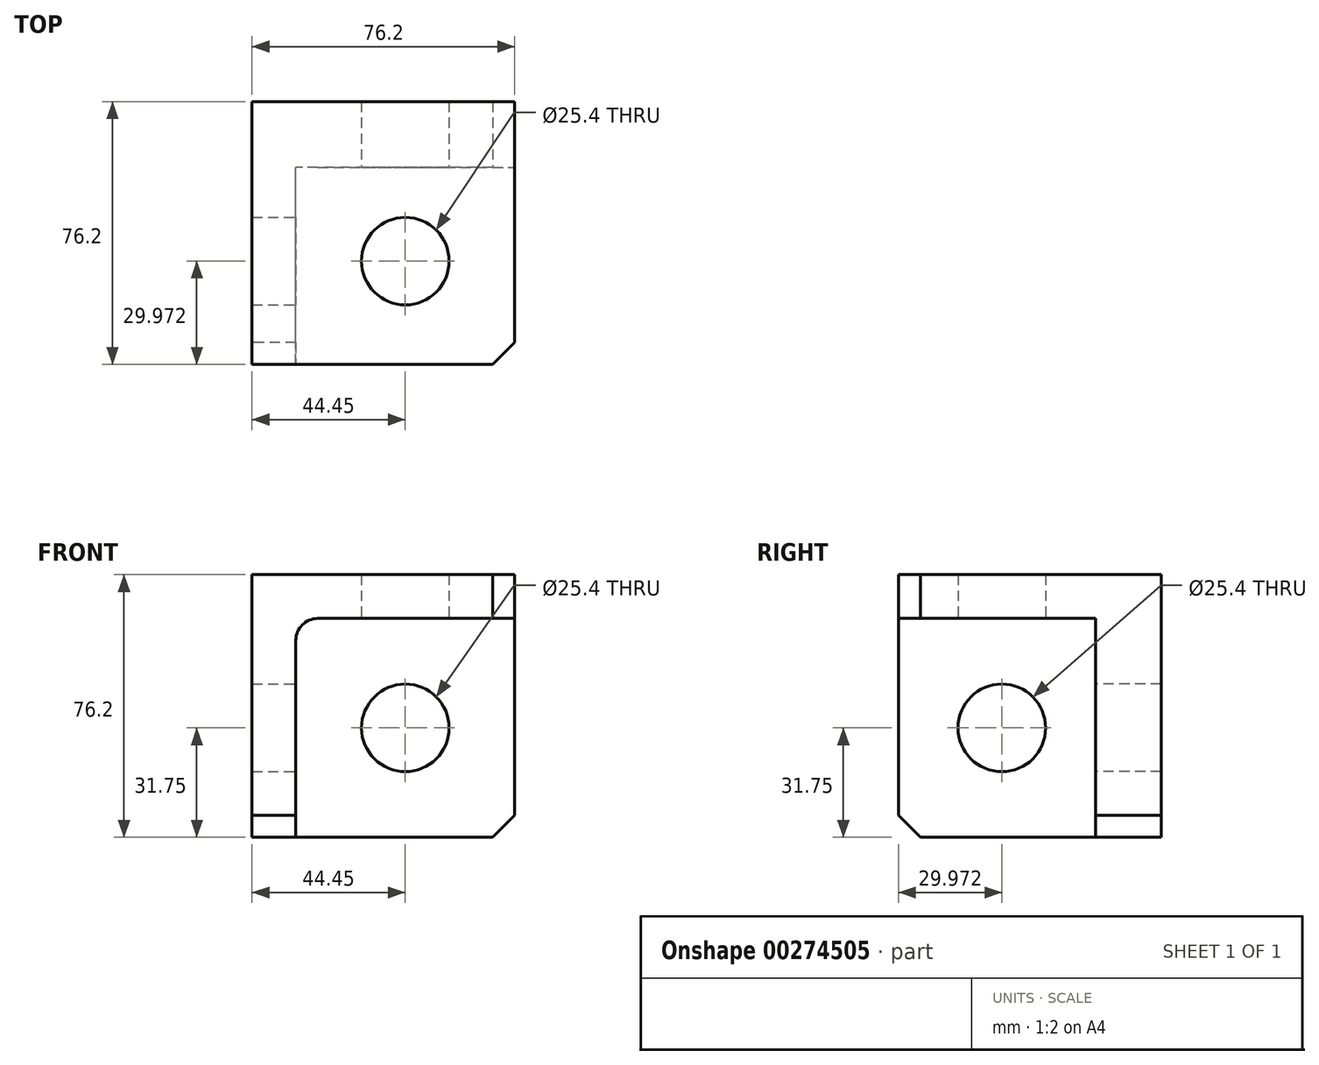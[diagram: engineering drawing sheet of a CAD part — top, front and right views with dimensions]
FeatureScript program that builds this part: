
annotation { "Feature Type Name" : "Feature", "Feature Type Description" : "" }
export const myFeature = defineFeature(function(context is Context, id is Id, definition is map)
    precondition{}
    {
        {
            var Q0;
            Q0=qCreatedBy(makeId("Front.planeOp"),FACE);
            var sketch = newSketch(context, id + "F0", { "sketchPlane" : qUnion([Q0])});
            skLineSegment(sketch, "E0.bottom", {"start": v(0, 0) * mm, "end": v(-76.2, 0) * mm});
            skLineSegment(sketch, "E0.top", {"start": v(0, 76.2) * mm, "end": v(-76.2, 76.2) * mm});
            skLineSegment(sketch, "E0.left", {"start": v(0, 0) * mm, "end": v(0, 76.2) * mm});
            skLineSegment(sketch, "E0.right", {"start": v(-76.2, 0) * mm, "end": v(-76.2, 76.2) * mm});
            skSolve(sketch);
        }
        {
            var Q0;
            Q0=makeQuery(id+"F0.imprint","IMPRINT",FACE,{"disambiguationData":[TD([[makeQuery(id+"F0.imprint","IMPRINT",EDGE,{"derivedFrom":sQuery(id+"F0.wireOp",EDGE,"E0.bottom")}),-1.0]])]});
            extrude(context, id + "F1", {"entities" : qUnion([Q0]), "depth" : 19.05 * mm});
        }
        {
            var Q0;
            Q0=makeQuery(id+"F1.opExtrude","CAP_FACE",FACE,{"disambiguationData":[OSD([sQuery(id+"F0.wireOp",EDGE,"E0.bottom"),sQuery(id+"F0.wireOp",EDGE,"E0.top"),sQuery(id+"F0.wireOp",EDGE,"E0.left"),sQuery(id+"F0.wireOp",EDGE,"E0.right")])],"isStart":false});
            var sketch = newSketch(context, id + "F2", { "sketchPlane" : qUnion([Q0])});
            skLineSegment(sketch, "E1", {"start": v(-76.2, 0) * mm, "end": v(-76.2, 76.2) * mm});
            skLineSegment(sketch, "E2", {"start": v(-76.2, 76.2) * mm, "end": v(0, 76.2) * mm});
            skLineSegment(sketch, "E3", {"start": v(0, 76.2) * mm, "end": v(0, 63.5) * mm});
            skLineSegment(sketch, "E4", {"start": v(-76.2, 0) * mm, "end": v(-63.5, 0) * mm});
            skLineSegment(sketch, "E5", {"start": v(-63.5, 0) * mm, "end": v(-63.5, 63.5) * mm});
            skLineSegment(sketch, "E6", {"start": v(-63.5, 63.5) * mm, "end": v(0, 63.5) * mm});
            skSolve(sketch);
        }
        {
            var Q0;
            Q0=makeQuery(id+"F2.imprint","IMPRINT",FACE,{"disambiguationData":[TD([[makeQuery(id+"F2.imprint","IMPRINT",EDGE,{"derivedFrom":sQuery(id+"F2.wireOp",EDGE,"E1")}),-1.0]])]});
            extrude(context, id + "F3", {"entities" : qUnion([Q0]), "operationType" : NewBodyOperationType.ADD, "depth" : 57.15 * mm});
        }
        {
            var Q0;
            Q0=makeQuery(id+"F3.opExtrude","SWEPT_FACE",FACE,{"disambiguationData":[OSD([sQuery(id+"F2.wireOp",EDGE,"E6")])]});
            var sketch = newSketch(context, id + "F4", { "sketchPlane" : qUnion([Q0])});
            skCircle(sketch, "E7", {"center": v(-31.75, 46.23) * mm, "radius": 12.7 * mm});
            skSolve(sketch);
        }
        {
            var Q0;
            Q0=makeQuery(id+"F4.imprint","IMPRINT",FACE,{"disambiguationData":[TD([[makeQuery(id+"F4.imprint","IMPRINT",EDGE,{"derivedFrom":sQuery(id+"F4.wireOp",EDGE,"E7")}),1.0]])]});
            extrude(context, id + "F5", {"entities" : qUnion([Q0]), "operationType" : NewBodyOperationType.REMOVE, "oppositeDirection" : true, "depth" : 12.7 * mm});
        }
        {
            var Q0;
            Q0=makeQuery(id+"F1.opExtrude","CAP_FACE",FACE,{"disambiguationData":[OSD([sQuery(id+"F0.wireOp",EDGE,"E0.bottom"),sQuery(id+"F0.wireOp",EDGE,"E0.top"),sQuery(id+"F0.wireOp",EDGE,"E0.left"),sQuery(id+"F0.wireOp",EDGE,"E0.right")])],"isStart":false});
            var sketch = newSketch(context, id + "F6", { "sketchPlane" : qUnion([Q0])});
            skCircle(sketch, "E8", {"center": v(-31.75, 31.75) * mm, "radius": 12.7 * mm});
            skSolve(sketch);
        }
        {
            var Q0;
            Q0 = qSketchRegion(id + "F6", true);
            extrude(context, id + "F7", {"entities" : qUnion([Q0]), "operationType" : NewBodyOperationType.REMOVE, "oppositeDirection" : true, "depth" : 19.05 * mm});
        }
        {
            var Q0;
            Q0=makeQuery(id+"F3.opExtrude","SWEPT_EDGE",EDGE,{"disambiguationData":[OSD([sQuery(id+"F2.wireOp",EDGE,"E5"),sQuery(id+"F2.wireOp",EDGE,"E6")])]});
            fillet(context, id + "F8", {"entities" : qUnion([Q0]), "radius" : 6.35 * mm, "tangentPropagation" : true, "allowEdgeOverflow" : false});
        }
        {
            var Q0;
            Q0=makeQuery(id+"F1.opExtrude","SWEPT_EDGE",EDGE,{"disambiguationData":[OSD([sQuery(id+"F0.wireOp",EDGE,"E0.bottom"),sQuery(id+"F0.wireOp",EDGE,"E0.left")])]});
            var Q1;
            Q1=makeQuery(id+"F3.opExtrude","CAP_EDGE",EDGE,{"disambiguationData":[OSD([sQuery(id+"F2.wireOp",EDGE,"E4")])],"isStart":false});
            var Q2;
            Q2=makeQuery(id+"F3.opExtrude","CAP_EDGE",EDGE,{"disambiguationData":[OSD([sQuery(id+"F2.wireOp",EDGE,"E3")])],"isStart":false});
            chamfer(context, id + "F9", {"entities" : qUnion([Q0, Q1, Q2]), "width" : 6.35 * mm, "tangentPropagation" : true});
        }
        {
            var Q0;
            Q0=makeQuery(id+"F3.opExtrude","SWEPT_FACE",FACE,{"disambiguationData":[OSD([sQuery(id+"F2.wireOp",EDGE,"E5")])]});
            var sketch = newSketch(context, id + "F10", { "sketchPlane" : qUnion([Q0])});
            skCircle(sketch, "E9", {"center": v(-46.23, 31.75) * mm, "radius": 12.7 * mm});
            skSolve(sketch);
        }
        {
            var Q0;
            Q0 = qSketchRegion(id + "F10", true);
            extrude(context, id + "F11", {"entities" : qUnion([Q0]), "operationType" : NewBodyOperationType.REMOVE, "oppositeDirection" : true, "depth" : 12.7 * mm});
        }
    });
